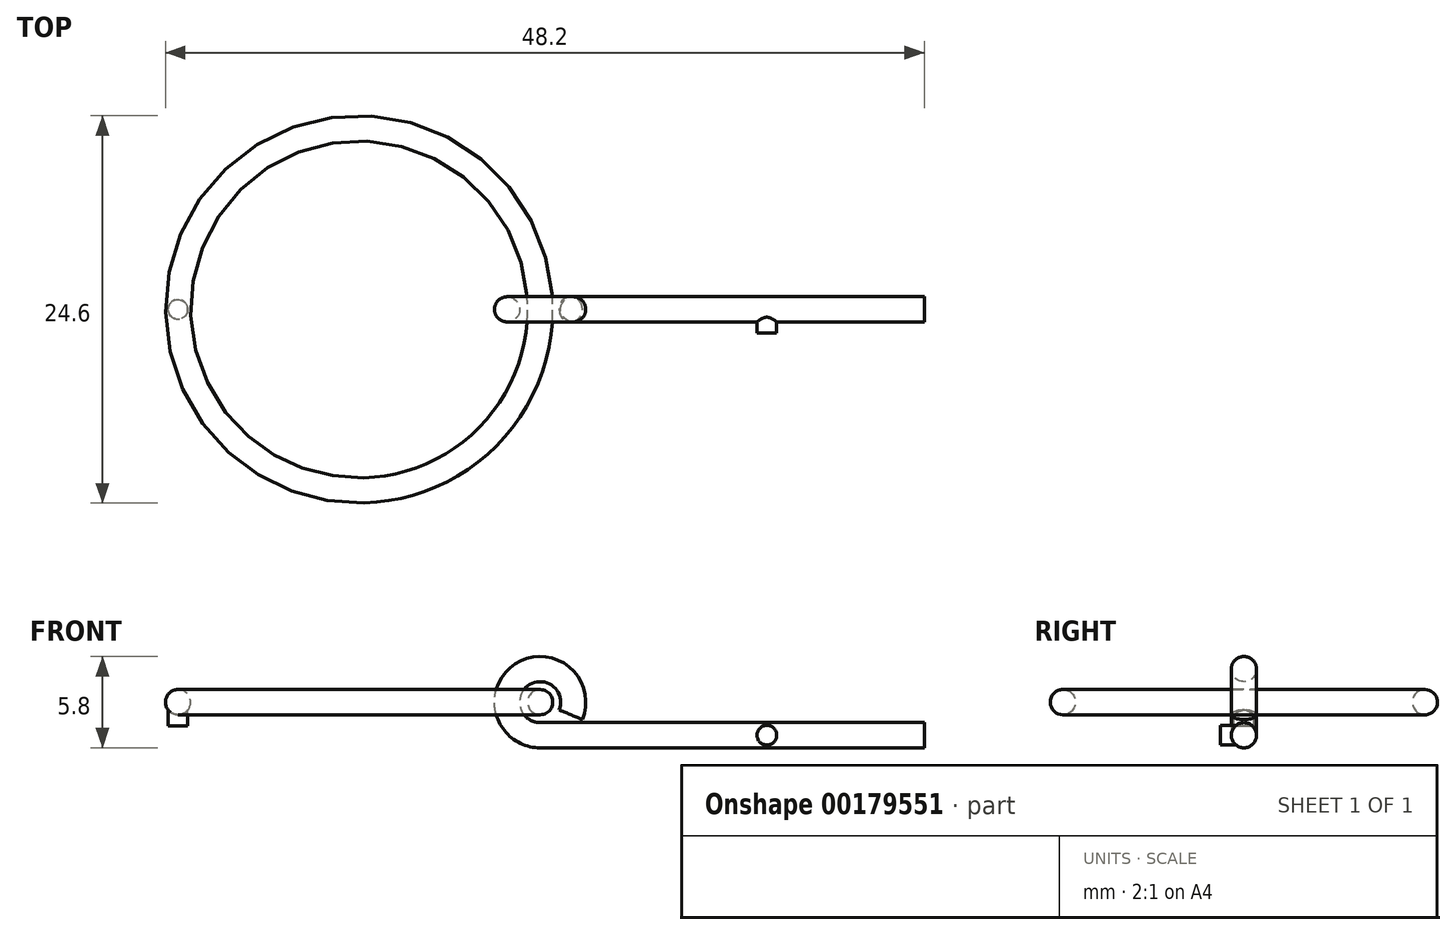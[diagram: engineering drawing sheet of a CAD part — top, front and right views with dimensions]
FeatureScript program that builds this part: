
annotation { "Feature Type Name" : "Feature", "Feature Type Description" : "" }
export const myFeature = defineFeature(function(context is Context, id is Id, definition is map)
    precondition{}
    {
        {
            var Q0;
            Q0=qCreatedBy(makeId("Front.planeOp"),FACE);
            var sketch = newSketch(context, id + "F0", { "sketchPlane" : qUnion([Q0])});
            skLineSegment(sketch, "E0", {"start": v(0, 0) * mm, "end": v(-24.4, 0) * mm});
            skArc(sketch, "E1", {"start": v(-24.4, 0) * mm, "mid": v(-25.57, 3.84) * mm, "end": v(-22.46, 1.3) * mm});
            skSolve(sketch);
        }
        {
            var Q0;
            Q0=qCreatedBy(makeId("Right.planeOp"),FACE);
            var sketch = newSketch(context, id + "F1", { "sketchPlane" : qUnion([Q0])});
            skCircle(sketch, "E2", {"center": v(0, 0) * mm, "radius": 0.8 * mm});
            skSolve(sketch);
        }
        {
            var Q0;
            Q0 = qSketchRegion(id + "F1", true);
            var Q1;
            Q1=sQuery(id+"F0.wireOp",EDGE,"E0");
            var Q2;
            Q2=sQuery(id+"F0.wireOp",EDGE,"E1");
            sweep(context, id + "F2", {"profiles" : qUnion([Q0]), "path" : qUnion([Q1, Q2])});
        }
        {
            var Q0;
            Q0=qCreatedBy(makeId("Top.planeOp"),FACE);
            cPlane(context, id + "F3", {"entities" : qUnion([Q0]), "cplaneType" : CPlaneType.OFFSET, "offset" : 2.1 * mm, "width" : 150 * mm, "height" : 150 * mm});
        }
        {
            var Q0;
            Q0=qCreatedBy(id+"F3.planeOp",FACE);
            var sketch = newSketch(context, id + "F4", { "sketchPlane" : qUnion([Q0])});
            skCircle(sketch, "E3", {"center": v(-35.9, 0) * mm, "radius": 11.5 * mm});
            skSolve(sketch);
        }
        {
            var Q0;
            Q0=qCreatedBy(makeId("Front.planeOp"),FACE);
            var sketch = newSketch(context, id + "F5", { "sketchPlane" : qUnion([Q0])});
            skCircle(sketch, "E4", {"center": v(-24.4, 2.1) * mm, "radius": 0.8 * mm});
            skSolve(sketch);
        }
        {
            var Q0;
            Q0 = qSketchRegion(id + "F5", true);
            var Q1;
            Q1=sQuery(id+"F4.wireOp",EDGE,"E3");
            sweep(context, id + "F6", {"operationType" : NewBodyOperationType.ADD, "profiles" : qUnion([Q0]), "path" : qUnion([Q1])});
        }
        {
            var Q0;
            Q0=qCreatedBy(makeId("Front.planeOp"),FACE);
            var sketch = newSketch(context, id + "F7", { "sketchPlane" : qUnion([Q0])});
            skCircle(sketch, "E5", {"center": v(-10, 0) * mm, "radius": 0.62 * mm});
            skSolve(sketch);
        }
        {
            var Q0;
            Q0 = qSketchRegion(id + "F7", true);
            extrude(context, id + "F8", {"entities" : qUnion([Q0]), "operationType" : NewBodyOperationType.ADD, "depth" : 1.5 * mm});
        }
        {
            var Q0;
            Q0=qCreatedBy(id+"F3.planeOp",FACE);
            var sketch = newSketch(context, id + "F9", { "sketchPlane" : qUnion([Q0])});
            skCircle(sketch, "E6", {"center": v(-47.4, 0) * mm, "radius": 0.62 * mm});
            skSolve(sketch);
        }
        {
            var Q0;
            Q0 = qSketchRegion(id + "F9", true);
            extrude(context, id + "F10", {"entities" : qUnion([Q0]), "operationType" : NewBodyOperationType.ADD, "oppositeDirection" : true, "depth" : 1.5 * mm});
        }
    });
